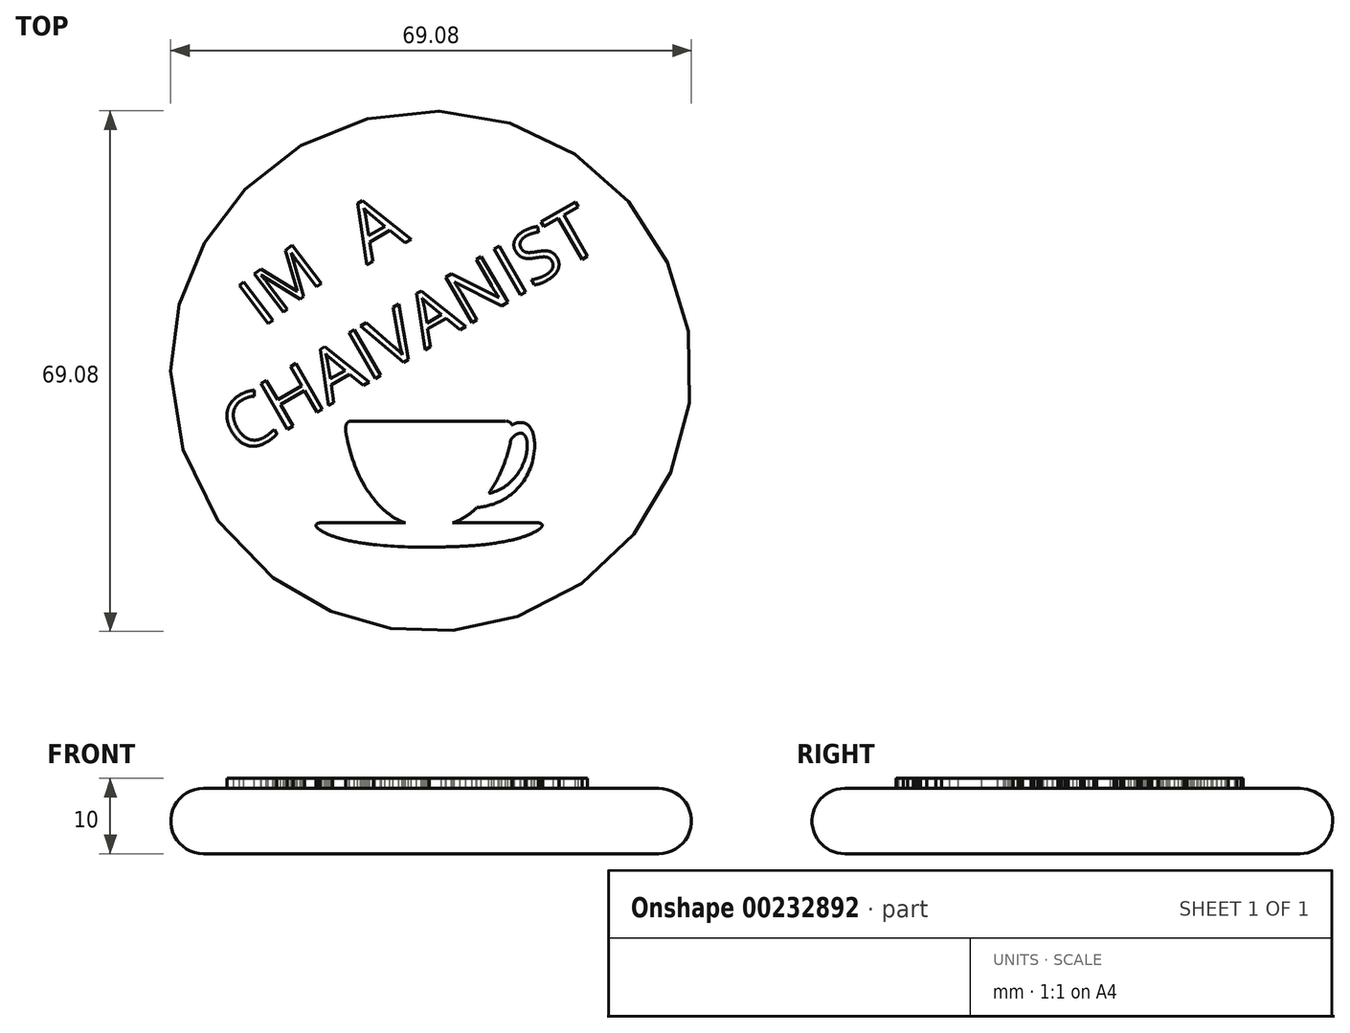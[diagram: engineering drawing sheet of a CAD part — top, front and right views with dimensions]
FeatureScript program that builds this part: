
annotation { "Feature Type Name" : "Feature", "Feature Type Description" : "" }
export const myFeature = defineFeature(function(context is Context, id is Id, definition is map)
    precondition{}
    {
        {
            var Q0;
            Q0=qCreatedBy(makeId("Front.planeOp"),FACE);
            var sketch = newSketch(context, id + "F0", { "sketchPlane" : qUnion([Q0])});
            skLineSegment(sketch, "E0.bottom", {"start": v(0, 0) * mm, "end": v(-30.2, 0) * mm});
            skLineSegment(sketch, "E0.top", {"start": v(0, 8.68) * mm, "end": v(-30.2, 8.68) * mm});
            skLineSegment(sketch, "E0.left", {"start": v(0, 0) * mm, "end": v(0, 8.68) * mm});
            skLineSegment(sketch, "E0.right", {"start": v(-30.2, 0) * mm, "end": v(-30.2, 8.68) * mm});
            skArc(sketch, "E1", {"start": v(-30.2, 8.68) * mm, "mid": v(-34.54, 4.34) * mm, "end": v(-30.2, 0) * mm});
            skSolve(sketch);
        }
        {
            var Q0;
            Q0 = qSketchRegion(id + "F0", true);
            var Q1;
            Q1=sQuery(id+"F0.wireOp",EDGE,"E0.left");
            revolve(context, id + "F1", {"entities" : qUnion([Q0]), "axis" : qUnion([Q1]), "revolveType" : RevolveType.FULL});
        }
        {
            var Q0;
            Q0=qCreatedBy(makeId("Top.planeOp"),FACE);
            cPlane(context, id + "F2", {"entities" : qUnion([Q0]), "cplaneType" : CPlaneType.OFFSET, "offset" : 10 * mm, "width" : 152.4 * mm, "height" : 152.4 * mm});
        }
        {
            var Q0;
            Q0=qCreatedBy(id+"F2.planeOp",FACE);
            var sketch = newSketch(context, id + "F3", { "sketchPlane" : qUnion([Q0])});
            skArc(sketch, "E2", {"start": v(14.58, -20.22) * mm, "mid": v(14.4, -20.16) * mm, "end": v(14.2, -20.14) * mm});
            skArc(sketch, "E3", {"start": v(14.74, -20.53) * mm, "mid": v(14.72, -20.34) * mm, "end": v(14.58, -20.22) * mm});
            skArc(sketch, "E4", {"start": v(14.54, -20.83) * mm, "mid": v(14.66, -20.7) * mm, "end": v(14.74, -20.53) * mm});
            skArc(sketch, "E5", {"start": v(14.24, -21.07) * mm, "mid": v(14.4, -20.96) * mm, "end": v(14.54, -20.83) * mm});
            skArc(sketch, "E6", {"start": v(12.57, -21.87) * mm, "mid": v(13.43, -21.51) * mm, "end": v(14.24, -21.07) * mm});
            skArc(sketch, "E7", {"start": v(10.8, -22.4) * mm, "mid": v(11.7, -22.16) * mm, "end": v(12.57, -21.87) * mm});
            skArc(sketch, "E8", {"start": v(7.14, -23) * mm, "mid": v(8.98, -22.75) * mm, "end": v(10.8, -22.4) * mm});
            skArc(sketch, "E9", {"start": v(3.45, -23.28) * mm, "mid": v(5.3, -23.17) * mm, "end": v(7.14, -23) * mm});
            skArc(sketch, "E10", {"start": v(-0.26, -23.34) * mm, "mid": v(1.6, -23.33) * mm, "end": v(3.45, -23.28) * mm});
            skArc(sketch, "E11", {"start": v(-7.66, -23) * mm, "mid": v(-3.96, -23.3) * mm, "end": v(-0.26, -23.34) * mm});
            skArc(sketch, "E12", {"start": v(-11.31, -22.4) * mm, "mid": v(-9.5, -22.76) * mm, "end": v(-7.66, -23) * mm});
            skArc(sketch, "E13", {"start": v(-13.09, -21.87) * mm, "mid": v(-12.2, -22.16) * mm, "end": v(-11.31, -22.4) * mm});
            skArc(sketch, "E14", {"start": v(-14.75, -21.07) * mm, "mid": v(-13.95, -21.52) * mm, "end": v(-13.09, -21.87) * mm});
            skArc(sketch, "E15", {"start": v(-15.05, -20.83) * mm, "mid": v(-14.9, -20.96) * mm, "end": v(-14.75, -21.07) * mm});
            skArc(sketch, "E16", {"start": v(-15.26, -20.52) * mm, "mid": v(-15.18, -20.7) * mm, "end": v(-15.05, -20.83) * mm});
            skArc(sketch, "E17", {"start": v(-15.08, -20.22) * mm, "mid": v(-15.21, -20.35) * mm, "end": v(-15.26, -20.52) * mm});
            skArc(sketch, "E18", {"start": v(-14.72, -20.14) * mm, "mid": v(-14.9, -20.16) * mm, "end": v(-15.08, -20.22) * mm});
            skLineSegment(sketch, "E19", {"start": v(-14.72, -20.14) * mm, "end": v(-3.37, -20.14) * mm});
            skArc(sketch, "E20", {"start": v(-5.08, -19.33) * mm, "mid": v(-4.25, -19.8) * mm, "end": v(-3.37, -20.14) * mm});
            skArc(sketch, "E21", {"start": v(-6.56, -18.14) * mm, "mid": v(-5.85, -18.77) * mm, "end": v(-5.08, -19.33) * mm});
            skArc(sketch, "E22", {"start": v(-8.88, -15.14) * mm, "mid": v(-7.82, -16.71) * mm, "end": v(-6.56, -18.14) * mm});
            skArc(sketch, "E23", {"start": v(-11.3, -7.98) * mm, "mid": v(-10.42, -11.67) * mm, "end": v(-8.88, -15.14) * mm});
            skArc(sketch, "E24", {"start": v(-11.25, -7.12) * mm, "mid": v(-11.33, -7.54) * mm, "end": v(-11.3, -7.98) * mm});
            skArc(sketch, "E25", {"start": v(-10.6, -6.63) * mm, "mid": v(-11.01, -6.76) * mm, "end": v(-11.25, -7.12) * mm});
            skLineSegment(sketch, "E26", {"start": v(-10.6, -6.63) * mm, "end": v(9.86, -6.63) * mm});
            skArc(sketch, "E27", {"start": v(10.73, -7.18) * mm, "mid": v(10.39, -6.75) * mm, "end": v(9.86, -6.63) * mm});
            skArc(sketch, "E28", {"start": v(11.89, -6.81) * mm, "mid": v(11.28, -6.9) * mm, "end": v(10.73, -7.18) * mm});
            skArc(sketch, "E29", {"start": v(12.8, -7.12) * mm, "mid": v(12.37, -6.89) * mm, "end": v(11.89, -6.81) * mm});
            skArc(sketch, "E30", {"start": v(13.4, -7.9) * mm, "mid": v(13.14, -7.48) * mm, "end": v(12.8, -7.12) * mm});
            skArc(sketch, "E31", {"start": v(13.74, -9.84) * mm, "mid": v(13.66, -8.85) * mm, "end": v(13.4, -7.9) * mm});
            skArc(sketch, "E32", {"start": v(11.55, -15.49) * mm, "mid": v(13.18, -12.87) * mm, "end": v(13.74, -9.84) * mm});
            skArc(sketch, "E33", {"start": v(9.07, -17.32) * mm, "mid": v(10.4, -16.53) * mm, "end": v(11.55, -15.49) * mm});
            skArc(sketch, "E34", {"start": v(6.1, -18.1) * mm, "mid": v(7.62, -17.84) * mm, "end": v(9.07, -17.32) * mm});
            skArc(sketch, "E35", {"start": v(4.6, -19.31) * mm, "mid": v(5.37, -18.75) * mm, "end": v(6.1, -18.1) * mm});
            skArc(sketch, "E36", {"start": v(2.85, -20.14) * mm, "mid": v(3.75, -19.8) * mm, "end": v(4.6, -19.31) * mm});
            skLineSegment(sketch, "E37", {"start": v(2.85, -20.14) * mm, "end": v(14.2, -20.14) * mm});
            skArc(sketch, "E38", {"start": v(7.65, -16.24) * mm, "mid": v(9.68, -15.4) * mm, "end": v(11.29, -13.91) * mm});
            skArc(sketch, "E39", {"start": v(7.65, -16.24) * mm, "mid": v(8.67, -14.59) * mm, "end": v(9.49, -12.83) * mm});
            skArc(sketch, "E40", {"start": v(9.49, -12.83) * mm, "mid": v(10.13, -11) * mm, "end": v(10.6, -9.12) * mm});
            skArc(sketch, "E41", {"start": v(11.12, -8.52) * mm, "mid": v(10.84, -8.8) * mm, "end": v(10.6, -9.12) * mm});
            skArc(sketch, "E42", {"start": v(11.84, -8.22) * mm, "mid": v(11.46, -8.32) * mm, "end": v(11.12, -8.52) * mm});
            skArc(sketch, "E43", {"start": v(12.31, -8.4) * mm, "mid": v(12.1, -8.27) * mm, "end": v(11.84, -8.22) * mm});
            skArc(sketch, "E44", {"start": v(12.6, -8.83) * mm, "mid": v(12.48, -8.6) * mm, "end": v(12.31, -8.4) * mm});
            skArc(sketch, "E45", {"start": v(12.76, -9.84) * mm, "mid": v(12.74, -9.32) * mm, "end": v(12.6, -8.83) * mm});
            skArc(sketch, "E46", {"start": v(12.35, -11.99) * mm, "mid": v(12.66, -10.93) * mm, "end": v(12.76, -9.84) * mm});
            skArc(sketch, "E47", {"start": v(11.29, -13.91) * mm, "mid": v(11.89, -13) * mm, "end": v(12.35, -11.99) * mm});
            skSolve(sketch);
        }
        {
            var Q0;
            Q0 = qSketchRegion(id + "F3", true);
            extrude(context, id + "F4", {"entities" : qUnion([Q0]), "operationType" : NewBodyOperationType.ADD, "oppositeDirection" : true, "depth" : 3 * mm});
        }
        {
            var Q0;
            Q0=qCreatedBy(id+"F2.planeOp",FACE);
            var sketch = newSketch(context, id + "F5", { "sketchPlane" : qUnion([Q0])});
            skText(sketch, "E48", { "text": "IM", "fontName": "OpenSans-Regular.ttf"});
            skText(sketch, "E49", { "text": "A", "fontName": "OpenSans-Regular.ttf"});
            skText(sketch, "E50", { "text": "CHAIVANIST", "fontName": "OpenSans-Regular.ttf"});
            const initialGuessF5  = {"E48": [-0.02228, 0.00578, 0.79506, 0.60654, 0.00643], "E49": [-0.0085, 0.0141, 0.86603, 0.5, 0.00771], "E50": [-0.02524, -0.0113, 0.86603, 0.5, 0.00707]};
            skSetInitialGuess(sketch, initialGuessF5);
            skSolve(sketch);
        }
        {
            var Q0;
            Q0 = qSketchRegion(id + "F5", true);
            extrude(context, id + "F6", {"entities" : qUnion([Q0]), "operationType" : NewBodyOperationType.ADD, "oppositeDirection" : true, "depth" : 3 * mm});
        }
    });
